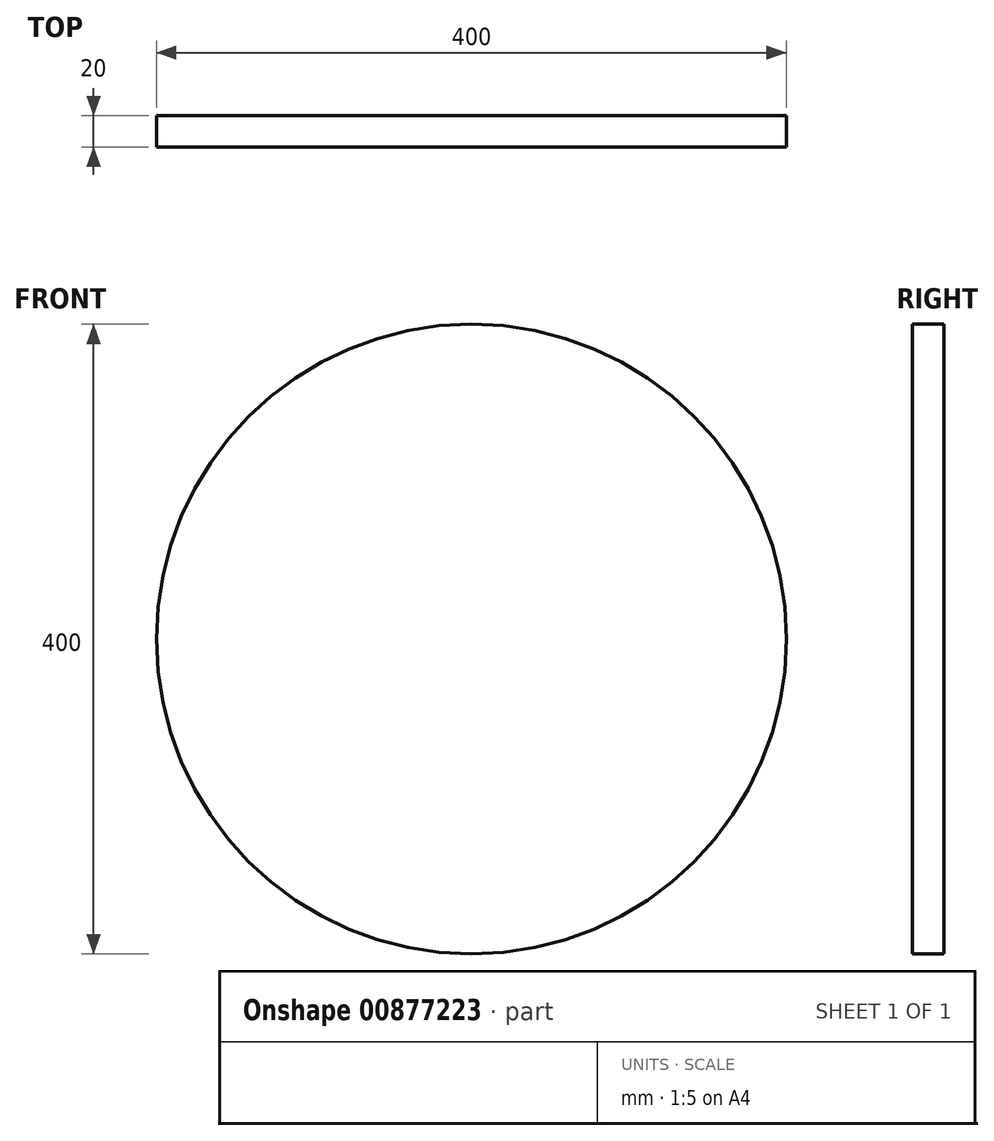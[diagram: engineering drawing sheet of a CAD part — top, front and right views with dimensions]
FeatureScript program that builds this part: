
annotation { "Feature Type Name" : "Feature", "Feature Type Description" : "" }
export const myFeature = defineFeature(function(context is Context, id is Id, definition is map)
    precondition{}
    {
        {
            var Q0;
            Q0=qCreatedBy(makeId("Front.planeOp"),FACE);
            var sketch = newSketch(context, id + "F0", { "sketchPlane" : qUnion([Q0])});
            skCircle(sketch, "E0", {"center": v(0, 0) * mm, "radius": 200 * mm});
            skSolve(sketch);
        }
        {
            var Q0;
            Q0 = qSketchRegion(id + "F0", true);
            extrude(context, id + "F1", {"entities" : qUnion([Q0]), "depth" : 20 * mm, "offsetDistance" : 25 * mm});
        }
    });
